# Revit family: РИДАН_BVR-СR_Кран шаровой ГОСТ с насадкой для шланга
name_source: partatom
category: Арматура трубопроводов
units: mm (PartAtom-declared; Revit-internal decimal feet)

## family parameters
Всегда вертикально = Да
На основе рабочей плоскости = Нет
Общий = Нет
При загрузке вырезать с полостями = Нет
Размер круглого соединителя = Использовать диаметр
Тип детали = Торцовая крышка

## types (3) — shared parameters
ADSK_Версия Revit = 2019
ADSK_Версия семейства = 1.0
ADSK_Единица измерения = шт.
ADSK_Завод-изготовитель = ООО «Ридан-Трейд»
ADSK_Количество = 1
ADSK_Материал = Латунь Никелированная
LT = BVR-CR
URL = https://ridan.ru
c = 1 мм
h = 5 мм
z = 10 мм

## per-type parameters (varying)
- DN15: ADSK_Диаметр условный=15 мм; ADSK_Код изделия=065B8300RG; ADSK_Марка=BVR-CR DN15; ADSK_Масса=0.25; ADSK_Наименование=Кран шаровой ГОСТ BVR-CR с насадкой для шланга PN10, Tmax=95C, DN15; a=5 мм; b=11 мм; d=10 мм; e=1 мм; f=21 мм; g=1 мм; i=12 мм; j=1 мм; k=18 мм; l=19 мм; m=21 мм; n=23 мм; o=23 мм; p=23 мм; q=21 мм; r=14 мм; s=23 мм; t=15 мм; u=8 мм; v=11 мм; w=18 мм; x=12 мм; y=80 мм; УГО_Длина=80 мм
- DN20: ADSK_Диаметр условный=20 мм; ADSK_Код изделия=065B8301RG; ADSK_Марка=BVR-CR DN20; ADSK_Масса=0.29; ADSK_Наименование=Кран шаровой ГОСТ BVR-CR с насадкой для шланга PN10, Tmax=95C, DN20; a=6 мм; b=12 мм; d=12 мм; e=1 мм; f=22 мм; g=2 мм; i=11 мм; j=1 мм; k=20 мм; l=24 мм; m=27 мм; n=28 мм; o=28 мм; p=25 мм; q=23 мм; r=17 мм; s=24 мм; t=15 мм; u=10 мм; v=15 мм; w=23 мм; x=15 мм; y=87 мм; УГО_Длина=87 мм
- DN25: ADSK_Диаметр условный=25 мм; ADSK_Код изделия=065B8302RG; ADSK_Марка=BVR-CR DN25; ADSK_Масса=0.5; ADSK_Наименование=Кран шаровой ГОСТ BVR-CR с насадкой для шланга PN10, Tmax=95C, DN25; a=8 мм; b=12 мм; d=14 мм; e=2 мм; f=26 мм; g=3 мм; i=14 мм; j=2 мм; k=25 мм; l=30 мм; m=33 мм; n=36 мм; o=36 мм; p=34 мм; q=33 мм; r=24 мм; s=30 мм; t=17 мм; u=8 мм; v=15 мм; w=27 мм; x=16 мм; y=100 мм; УГО_Длина=100 мм
